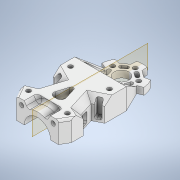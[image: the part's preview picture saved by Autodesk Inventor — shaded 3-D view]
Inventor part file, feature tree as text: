
AUTODESK INVENTOR PART (.ipt)
format: ipt  version: 2020 (Build 240168000, 168)  size: 579,072 bytes
history: native  units: mm
features: reference x15, sketch x12, extrude x9, thicken_offset x9, projected_geometry x7, other x7, fillet x6, mirror x4, chamfer x3, plane x2, loft x1, hole x1
ambient origin geometry x8: Origin, YZ Plane, XZ Plane, XY Plane, X Axis, Y Axis, Z Axis, Center Point
bodies: Solid1 (feature_tree)
feature tree (76):
  sketch  "Sketch1"  dims[d0=25.0mm d1=20.0mm]
  plane  "Work Plane1"
  extrude  "Extrusion1"  Depth=20.0mm
  extrude  "Extrusion2"  Depth=10.0mm TaperAngle=0.0deg
  extrude  "Extrusion3"  Depth=20.0mm TaperAngle=0.0deg
  thicken_offset  "Thicken1"
  thicken_offset  "Thicken2"
  extrude  "Extrusion4"  Depth=1.0mm
  loft  "Loft1"
  plane  "Work Plane2"
  mirror  "Mirror1"
  hole  "Hole1"  [1 undecoded]
  chamfer  "Chamfer2"  Angle=90.0deg  [1 undecoded]
  chamfer  "Chamfer3"  Angle=90.0deg  [1 undecoded]
  extrude  "Extrusion7"  Depth=2.0mm TaperAngle=60.0deg
  chamfer  "Chamfer4"  Distance=2.0mm Angle=60.0deg
  mirror  "Mirror3"
  fillet  "Fillet2"  Radius=20.0mm
  fillet  "Fillet3"  Radius=2.0mm
  thicken_offset  "Thicken3"
  extrude  "Extrusion9"  Depth=3.0mm
  extrude  "Extrusion10"  Depth=3.0mm
  mirror  "Mirror4"
  extrude  "Extrusion11"  Depth=3.0mm
  mirror  "Mirror5"
  fillet  "Fillet4"  Radius=5.585054mm
  fillet  "Fillet5"  Radius=5.585054mm
  fillet  "Fillet6"  Radius=12.0mm
  thicken_offset  "Thicken4"
  thicken_offset  "Thicken5"
  extrude  "Extrusion12"  Depth=2.0mm
  thicken_offset  "Thicken6"
  thicken_offset  "Thicken7"
  thicken_offset  "Thicken8"
  fillet  "Fillet7"  Radius=2.0mm
  thicken_offset  "Thicken9"
  reference  "Reference1"
  sketch  "Sketch2"  dims[d2=20.0mm d3=10.0mm d4=0.0mm]
  reference  "Reference2"
  reference  "Reference3"
  reference  "Reference4"
  reference  "Reference5"
  sketch  "Sketch3"  dims[d5=20.0mm d6=0.0mm d7=20.0mm d8=0.0mm]
  reference  "Reference6"
  sketch  "Sketch4"  dims[d9=1.0mm d10=1.0mm]
  reference  "Reference7"
  projected_geometry  "Projected Loop1"
  sketch  "Sketch6"  dims[d11=1.0mm d12=1.0mm]
  projected_geometry  "Projected Loop3"
  sketch  "Sketch7"  dims[d13=5.5mm d14=0.0mm d17=6.0mm]
  projected_geometry  "Projected Loop4"
  sketch  "Sketch9"  dims[d18=5.0mm]
  reference  "Reference13"
  reference  "Reference14"
  sketch  "Sketch10"  dims[d19=6.0mm d20=0.0mm d21=90.0deg d22=0.0mm d23=90.0deg]
  reference  "Reference15"
  reference  "Reference16"
  reference  "Reference17"
  reference  "Reference18"
  reference  "Reference19"
  sketch  "Sketch12"  dims[d29=4.2mm d30=5.98424mm d31=3.023mm d32=2.0mm d33=14.3117mm d34=5.0mm d35=0.0mm d36=4.5mm d37=2.0mm d38=60.0deg d39=4.5mm d40=2.0mm d41=60.0deg d43=20.0mm d44=0.0mm]
  projected_geometry  "Projected Loop7"
  sketch  "Sketch14"  dims[d45=6.0mm d46=2.0mm d47=60.0deg d48=2.0mm]
  projected_geometry  "Projected Loop9"
  projected_geometry  "Projected Loop10"
  sketch  "Sketch15"  dims[d53=3.0mm d57=1.0mm]
  projected_geometry  "Projected Loop11"
  sketch  "Sketch16"  dims[d58=1.0mm d59=25.0mm d60=32.0mm d61=5.585054mm d62=5.585054mm d63=12.0mm d64=0.0mm d66=2.0mm d67=2.0mm d68=2.0mm d69=2.0mm d70=6.0mm d71=0.0mm d72=2.0mm d73=2.0mm d74=2.0mm d75=6.0mm d76=3.0mm d77=0.0mm d78=1.5mm d79=1.5mm d80=3.0mm d81=1.0mm d82=1.0mm d83=1.0mm d84=1.0mm d85=20.0mm d86=0.0mm d87=1.0mm d88=1.0mm d89=1.0mm d90=1.0mm d91=2.0mm d92=2.0mm d93=3.0mm d94=1.0mm d95=1.0mm]
  reference  "Reference20"
  parser-record x2  (decoder bookkeeping rows leaked as tree rows — omitted from the tree; the rows remain in map.json)
  other  "sub_leg_1.iam"
  other  "joint_connector_4:1"
  other  "joint_connector_6:1"
  other  "sub_leg_1_lit.iam"
  other  "joint_connector_4_lit:1"
note: 3 required parameter values undecoded (feature->parameter linkage not recoverable at this tier; creation-order binding heuristic only, values carry confidence <= 0.55)
note: 2 file-system paths scrubbed to <path> (originals preserved in map.json)
